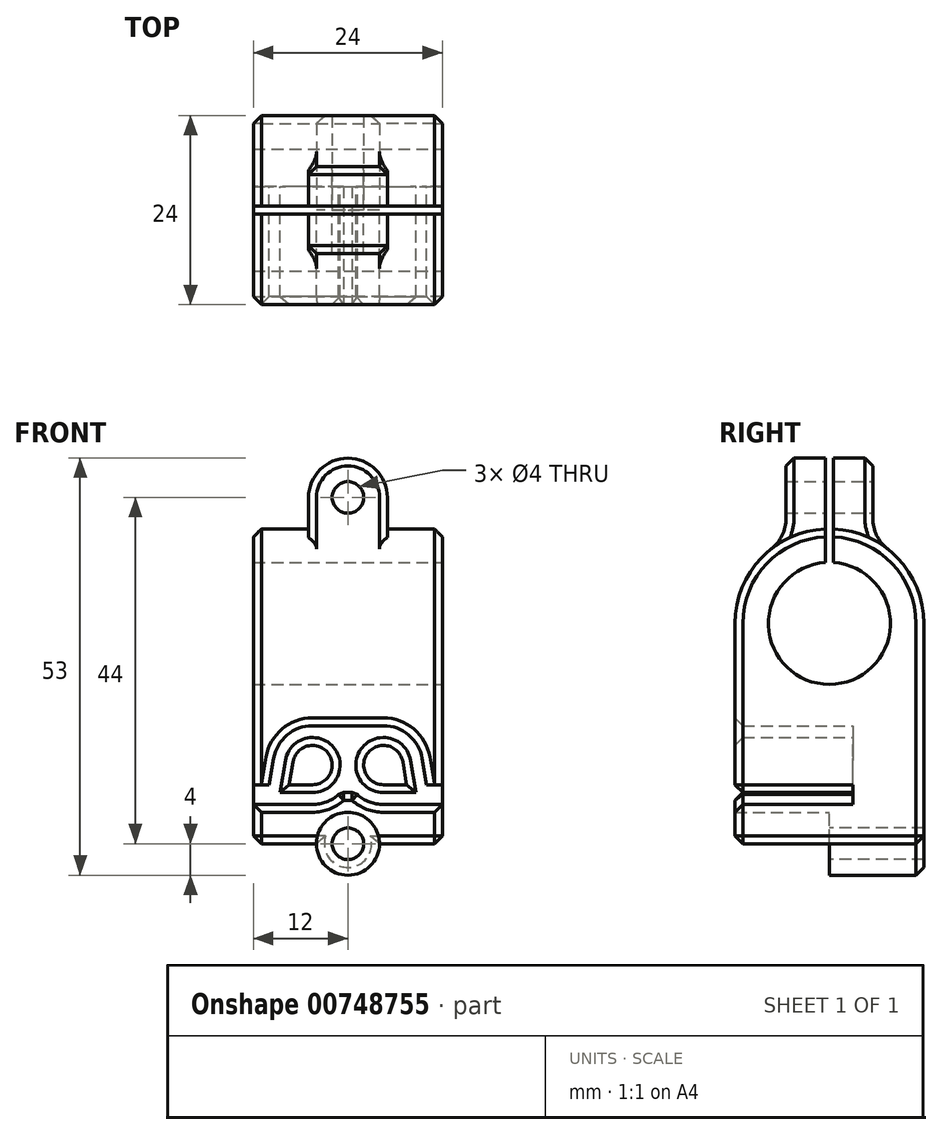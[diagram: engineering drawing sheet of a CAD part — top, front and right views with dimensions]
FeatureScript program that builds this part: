
annotation { "Feature Type Name" : "Feature", "Feature Type Description" : "" }
export const myFeature = defineFeature(function(context is Context, id is Id, definition is map)
    precondition{}
    {
        {
            var Q0;
            Q0=qCreatedBy(makeId("Front.planeOp"),FACE);
            var sketch = newSketch(context, id + "F0", { "sketchPlane" : qUnion([Q0])});
            skCircle(sketch, "E0", {"center": v(0, 0) * mm, "radius": 2 * mm});
            skCircle(sketch, "E1", {"center": v(0, 0) * mm, "radius": 4 * mm});
            skLineSegment(sketch, "E2", {"start": v(0, 0) * mm, "end": v(-12, 0) * mm});
            skLineSegment(sketch, "E3", {"start": v(-12, 0) * mm, "end": v(-12, 40) * mm});
            skLineSegment(sketch, "E4", {"start": v(-12, 40) * mm, "end": v(0, 40) * mm});
            skCircle(sketch, "E5", {"center": v(-4.5, 10) * mm, "radius": 3.5 * mm});
            skLineSegment(sketch, "E6", {"start": v(-12, 7.5) * mm, "end": v(-10, 7.5) * mm});
            skCircle(sketch, "E7", {"center": v(-4.5, 10) * mm, "radius": 5 * mm});
            skLineSegment(sketch, "E8", {"start": v(-4.5, 5) * mm, "end": v(-12, 5) * mm});
            skLineSegment(sketch, "E9", {"start": v(-12, 16) * mm, "end": v(0, 16) * mm});
            skLineSegment(sketch, "E10", {"start": v(0, 49) * mm, "end": v(-5, 49) * mm});
            skLineSegment(sketch, "E11", {"start": v(-5, 49) * mm, "end": v(-5, 40) * mm});
            skCircle(sketch, "E12", {"center": v(0, 44) * mm, "radius": 2 * mm});
            skLineSegment(sketch, "E13", {"start": v(0, 49) * mm, "end": v(0, -4) * mm});
            skLineSegment(sketch, "E14", {"start": v(-12, 28) * mm, "end": v(0, 28) * mm});
            skLineSegment(sketch, "E15", {"start": v(-5, 40) * mm, "end": v(-5, 28) * mm});
            skLineSegment(sketch, "E16", {"start": v(-4.5, 6.5) * mm, "end": v(-8.65, 6.5) * mm});
            skLineSegment(sketch, "E17", {"start": v(-8.65, 6.5) * mm, "end": v(-7.95, 10.59) * mm});
            skLineSegment(sketch, "E18", {"start": v(-10, 7.5) * mm, "end": v(-9.43, 10.84) * mm});
            skLineSegment(sketch, "E19", {"start": v(-4.5, 15) * mm, "end": v(0, 15) * mm});
            skLineSegment(sketch, "E20", {"start": v(-0.93, 6.5) * mm, "end": v(0, 6.5) * mm});
            skSolve(sketch);
        }
        {
            var Q0;
            {var subQ5=sQuery(id+"F0.wireOp",EDGE,"E10");Q0=makeQuery(id+"F0.imprint","IMPRINT",FACE,{"disambiguationData":[TD([[makeQuery(id+"F0.imprint","IMPRINT",EDGE,{"derivedFrom":subQ5}),1.0]])]});}
            var Q1;
            {var subQ3=sQuery(id+"F0.wireOp",EDGE,"E15");Q1=makeQuery(id+"F0.imprint","IMPRINT",FACE,{"disambiguationData":[TD([[makeQuery(id+"F0.imprint","IMPRINT",EDGE,{"derivedFrom":subQ3}),1.0]])]});}
            extrude(context, id + "F1", {"entities" : qUnion([Q0, Q1]), "endBound" : BoundingType.SYMMETRIC, "depth" : 11 * mm, "offsetDistance" : 25 * mm});
        }
        {
            var Q0;
            {var subQ1=sQuery(id+"F0.wireOp",EDGE,"E9");Q0=makeQuery(id+"F0.imprint","IMPRINT",FACE,{"disambiguationData":[TD([[makeQuery(id+"F0.imprint","IMPRINT",EDGE,{"derivedFrom":subQ1}),1.0]])]});}
            var Q1;
            Q1=sQuery(id+"F0.wireOp",EDGE,"E14");
            revolve(context, id + "F2", {"operationType" : NewBodyOperationType.ADD, "surfaceOperationType" : NewSurfaceOperationType.NEW, "entities" : qUnion([Q0]), "axis" : qUnion([Q1]), "revolveType" : RevolveType.FULL});
        }
        {
            var Q0;
            {var subQ1=sQuery(id+"F0.wireOp",EDGE,"E9");Q0=makeQuery(id+"F0.imprint","IMPRINT",FACE,{"disambiguationData":[TD([[makeQuery(id+"F0.imprint","IMPRINT",EDGE,{"derivedFrom":subQ1}),1.0]])]});}
            var Q1;
            {var subQ0=sQuery(id+"F0.wireOp",EDGE,"E6");Q1=makeQuery(id+"F0.imprint","IMPRINT",FACE,{"disambiguationData":[TD([[makeQuery(id+"F0.imprint","IMPRINT",EDGE,{"derivedFrom":subQ0}),1.0]])]});}
            var Q2;
            {var subQ0=sQuery(id+"F0.wireOp",EDGE,"D34r3Q79-cY7r-4sOT-R41t-FvUsecisL4TW");var subQ1=sQuery(id+"F0.wireOp",EDGE,"E5");var subQ2=makeQuery(id+"F0.imprint","INTERSECT",VERTEX,{"derivedFrom":[subQ1,subQ0]});Q2=makeQuery(id+"F0.imprint","IMPRINT",FACE,{"disambiguationData":[TD([[makeQuery(id+"F0.imprint","IMPRINT",EDGE,{"disambiguationData":[TD([[subQ2,1.0]])],"derivedFrom":subQ1}),-1.0]])]});}
            var Q3;
            {var subQ0=sQuery(id+"F0.wireOp",EDGE,"E5");var subQ1=makeQuery(id+"F0.imprint","INTERSECT",VERTEX,{"derivedFrom":[subQ0,sQuery(id+"F0.wireOp",EDGE,"D34r3Q79-cY7r-4sOT-R41t-FvUsecisL4TW")]});Q3=makeQuery(id+"F0.imprint","IMPRINT",FACE,{"disambiguationData":[TD([[makeQuery(id+"F0.imprint","IMPRINT",EDGE,{"disambiguationData":[TD([[subQ1,1.0]])],"derivedFrom":subQ0}),1.0]])]});}
            var Q4;
            {var subQ0=sQuery(id+"F0.wireOp",EDGE,"r9bTKT41-j5EP-3SKQ-5lYN-j0jZzXjLLhCI");var subQ1=sQuery(id+"F0.wireOp",EDGE,"D34r3Q79-cY7r-4sOT-R41t-FvUsecisL4TW");var subQ2=makeQuery(id+"F0.imprint","INTERSECT",VERTEX,{"derivedFrom":[subQ1,subQ0]});Q4=makeQuery(id+"F0.imprint","IMPRINT",FACE,{"disambiguationData":[TD([[makeQuery(id+"F0.imprint","IMPRINT",EDGE,{"disambiguationData":[TD([[subQ2,1.0]])],"derivedFrom":subQ1}),-1.0]])]});}
            var Q5;
            {var subQ3=sQuery(id+"F0.wireOp",EDGE,"E8");Q5=makeQuery(id+"F0.imprint","IMPRINT",FACE,{"disambiguationData":[TD([[makeQuery(id+"F0.imprint","IMPRINT",EDGE,{"derivedFrom":subQ3}),1.0]])]});}
            var Q6;
            {var subQ0=sQuery(id+"F0.wireOp",EDGE,"E17");var subQ1=sQuery(id+"F0.wireOp",EDGE,"E7");var subQ2=makeQuery(id+"F0.imprint","INTERSECT",VERTEX,{"derivedFrom":[subQ1,subQ0]});Q6=makeQuery(id+"F0.imprint","IMPRINT",FACE,{"disambiguationData":[TD([[makeQuery(id+"F0.imprint","IMPRINT",EDGE,{"disambiguationData":[TD([[subQ2,-1.0]])],"derivedFrom":subQ1}),-1.0]])]});}
            extrude(context, id + "F3", {"entities" : qUnion([Q0, Q1, Q2, Q3, Q4, Q5, Q6]), "operationType" : NewBodyOperationType.ADD, "depth" : 12 * mm, "offsetDistance" : 25 * mm});
        }
        {
            var Q0;
            {var subQ0=sQuery(id+"F0.wireOp",EDGE,"E6");Q0=makeQuery(id+"F0.imprint","IMPRINT",FACE,{"disambiguationData":[TD([[makeQuery(id+"F0.imprint","IMPRINT",EDGE,{"derivedFrom":subQ0}),1.0]])]});}
            var Q1;
            {var subQ0=sQuery(id+"F0.wireOp",EDGE,"E5");var subQ1=makeQuery(id+"F0.imprint","INTERSECT",VERTEX,{"derivedFrom":[subQ0,sQuery(id+"F0.wireOp",EDGE,"D34r3Q79-cY7r-4sOT-R41t-FvUsecisL4TW")]});Q1=makeQuery(id+"F0.imprint","IMPRINT",FACE,{"disambiguationData":[TD([[makeQuery(id+"F0.imprint","IMPRINT",EDGE,{"disambiguationData":[TD([[subQ1,1.0]])],"derivedFrom":subQ0}),1.0]])]});}
            var Q2;
            {var subQ1=sQuery(id+"F0.wireOp",EDGE,"E5");var subQ6=sQuery(id+"F0.wireOp",EDGE,"D34r3Q79-cY7r-4sOT-R41t-FvUsecisL4TW");var subQ7=makeQuery(id+"F0.imprint","INTERSECT",VERTEX,{"derivedFrom":[subQ1,subQ6]});Q2=makeQuery(id+"F0.imprint","IMPRINT",FACE,{"disambiguationData":[TD([[makeQuery(id+"F0.imprint","IMPRINT",EDGE,{"disambiguationData":[TD([[subQ7,-1.0]])],"derivedFrom":subQ1}),-1.0]])]});}
            var Q3;
            {var subQ0=sQuery(id+"F0.wireOp",EDGE,"D34r3Q79-cY7r-4sOT-R41t-FvUsecisL4TW");var subQ1=sQuery(id+"F0.wireOp",EDGE,"E5");var subQ2=makeQuery(id+"F0.imprint","INTERSECT",VERTEX,{"derivedFrom":[subQ1,subQ0]});Q3=makeQuery(id+"F0.imprint","IMPRINT",FACE,{"disambiguationData":[TD([[makeQuery(id+"F0.imprint","IMPRINT",EDGE,{"disambiguationData":[TD([[subQ2,1.0]])],"derivedFrom":subQ1}),-1.0]])]});}
            var Q4;
            {var subQ0=sQuery(id+"F0.wireOp",EDGE,"r9bTKT41-j5EP-3SKQ-5lYN-j0jZzXjLLhCI");var subQ1=sQuery(id+"F0.wireOp",EDGE,"D34r3Q79-cY7r-4sOT-R41t-FvUsecisL4TW");var subQ2=makeQuery(id+"F0.imprint","INTERSECT",VERTEX,{"derivedFrom":[subQ1,subQ0]});Q4=makeQuery(id+"F0.imprint","IMPRINT",FACE,{"disambiguationData":[TD([[makeQuery(id+"F0.imprint","IMPRINT",EDGE,{"disambiguationData":[TD([[subQ2,1.0]])],"derivedFrom":subQ1}),-1.0]])]});}
            var Q5;
            {var subQ1=sQuery(id+"F0.wireOp",EDGE,"E9");Q5=makeQuery(id+"F0.imprint","IMPRINT",FACE,{"disambiguationData":[TD([[makeQuery(id+"F0.imprint","IMPRINT",EDGE,{"derivedFrom":subQ1}),1.0]])]});}
            var Q6;
            {var subQ0=sQuery(id+"F0.wireOp",EDGE,"E17");var subQ1=sQuery(id+"F0.wireOp",EDGE,"E7");var subQ2=makeQuery(id+"F0.imprint","INTERSECT",VERTEX,{"derivedFrom":[subQ1,subQ0]});Q6=makeQuery(id+"F0.imprint","IMPRINT",FACE,{"disambiguationData":[TD([[makeQuery(id+"F0.imprint","IMPRINT",EDGE,{"disambiguationData":[TD([[subQ2,-1.0]])],"derivedFrom":subQ1}),-1.0]])]});}
            var Q7;
            {var subQ3=sQuery(id+"F0.wireOp",EDGE,"E8");Q7=makeQuery(id+"F0.imprint","IMPRINT",FACE,{"disambiguationData":[TD([[makeQuery(id+"F0.imprint","IMPRINT",EDGE,{"derivedFrom":subQ3}),1.0]])]});}
            var Q8;
            {var subQ6=sQuery(id+"F0.wireOp",EDGE,"E16");var subQ8=sQuery(id+"F0.wireOp",EDGE,"E5");var subQ9=makeQuery(id+"F0.imprint","INTERSECT",VERTEX,{"derivedFrom":[subQ8,subQ6]});Q8=makeQuery(id+"F0.imprint","IMPRINT",FACE,{"disambiguationData":[TD([[makeQuery(id+"F0.imprint","IMPRINT",EDGE,{"disambiguationData":[TD([[subQ9,-1.0]])],"derivedFrom":subQ8}),-1.0]])]});}
            var Q9;
            {var subQ4=sQuery(id+"F0.wireOp",EDGE,"E6");Q9=makeQuery(id+"F0.imprint","IMPRINT",FACE,{"disambiguationData":[TD([[makeQuery(id+"F0.imprint","IMPRINT",EDGE,{"derivedFrom":subQ4}),-1.0]])]});}
            var Q10;
            {var subQ0=sQuery(id+"F0.wireOp",EDGE,"E2");var subQ1=sQuery(id+"F0.wireOp",EDGE,"E0");var subQ2=makeQuery(id+"F0.imprint","INTERSECT",VERTEX,{"derivedFrom":[subQ1,subQ0]});Q10=makeQuery(id+"F0.imprint","IMPRINT",FACE,{"disambiguationData":[TD([[makeQuery(id+"F0.imprint","IMPRINT",EDGE,{"disambiguationData":[TD([[subQ2,-1.0]])],"derivedFrom":subQ1}),-1.0]])]});}
            var Q11;
            {var subQ0=sQuery(id+"F0.wireOp",EDGE,"E2");var subQ1=sQuery(id+"F0.wireOp",EDGE,"E0");var subQ2=makeQuery(id+"F0.imprint","INTERSECT",VERTEX,{"derivedFrom":[subQ1,subQ0]});Q11=makeQuery(id+"F0.imprint","IMPRINT",FACE,{"disambiguationData":[TD([[makeQuery(id+"F0.imprint","IMPRINT",EDGE,{"disambiguationData":[TD([[subQ2,1.0]])],"derivedFrom":subQ1}),-1.0]])]});}
            var Q12;
            {var subQ0=sQuery(id+"F0.wireOp",EDGE,"E19");Q12=makeQuery(id+"F0.imprint","IMPRINT",FACE,{"disambiguationData":[TD([[makeQuery(id+"F0.imprint","IMPRINT",EDGE,{"derivedFrom":subQ0}),-1.0]])]});}
            var Q13;
            {var subQ0=sQuery(id+"F0.wireOp",EDGE,"E20");Q13=makeQuery(id+"F0.imprint","IMPRINT",FACE,{"disambiguationData":[TD([[makeQuery(id+"F0.imprint","IMPRINT",EDGE,{"derivedFrom":subQ0}),1.0]])]});}
            extrude(context, id + "F4", {"entities" : qUnion([Q0, Q1, Q2, Q3, Q4, Q5, Q6, Q7, Q8, Q9, Q10, Q11, Q12, Q13]), "operationType" : NewBodyOperationType.ADD, "oppositeDirection" : true, "depth" : 12 * mm, "offsetDistance" : 25 * mm});
        }
        {
            var Q0;
            {var subQ4=sQuery(id+"F0.wireOp",EDGE,"E6");Q0=makeQuery(id+"F0.imprint","IMPRINT",FACE,{"disambiguationData":[TD([[makeQuery(id+"F0.imprint","IMPRINT",EDGE,{"derivedFrom":subQ4}),-1.0]])]});}
            var Q1;
            {var subQ6=sQuery(id+"F0.wireOp",EDGE,"E16");var subQ8=sQuery(id+"F0.wireOp",EDGE,"E5");var subQ9=makeQuery(id+"F0.imprint","INTERSECT",VERTEX,{"derivedFrom":[subQ8,subQ6]});Q1=makeQuery(id+"F0.imprint","IMPRINT",FACE,{"disambiguationData":[TD([[makeQuery(id+"F0.imprint","IMPRINT",EDGE,{"disambiguationData":[TD([[subQ9,-1.0]])],"derivedFrom":subQ8}),-1.0]])]});}
            var Q2;
            {var subQ0=sQuery(id+"F0.wireOp",EDGE,"E19");Q2=makeQuery(id+"F0.imprint","IMPRINT",FACE,{"disambiguationData":[TD([[makeQuery(id+"F0.imprint","IMPRINT",EDGE,{"derivedFrom":subQ0}),-1.0]])]});}
            var Q3;
            {var subQ0=sQuery(id+"F0.wireOp",EDGE,"E20");Q3=makeQuery(id+"F0.imprint","IMPRINT",FACE,{"disambiguationData":[TD([[makeQuery(id+"F0.imprint","IMPRINT",EDGE,{"derivedFrom":subQ0}),1.0]])]});}
            extrude(context, id + "F5", {"entities" : qUnion([Q0, Q1, Q2, Q3]), "operationType" : NewBodyOperationType.REMOVE, "oppositeDirection" : true, "depth" : 3 * mm, "offsetDistance" : 25 * mm});
        }
        {
            var Q0;
            {var subQ0=sQuery(id+"F0.wireOp",EDGE,"E13");var subQ1=makeQuery(id+"F0.imprint","INTERSECT",VERTEX,{"disambiguationData":[OD(1.0)],"derivedFrom":[sQuery(id+"F0.wireOp",EDGE,"E1"),subQ0]});var subQ2=makeQuery(id+"F0.imprint","INTERSECT",VERTEX,{"derivedFrom":[sQuery(id+"F0.wireOp",EDGE,"E9"),subQ0]});var subQ4=makeQuery(id+"F0.imprint","INTERSECT",VERTEX,{"derivedFrom":[sQuery(id+"F0.wireOp",EDGE,"E4"),subQ0]});Q0=makeQuery(id+"F4.boolean.opBoolean","MERGE",FACE,{"derivedFrom":[makeQuery(id+"F3.boolean.opBoolean","MERGE",FACE,{"derivedFrom":[makeQuery(id+"F2.boolean.opBoolean","MERGE",FACE,{"derivedFrom":[makeQuery(id+"F1.opExtrude","SWEPT_FACE",FACE,{"disambiguationData":[OSD([subQ0]),TDD([makeQuery(id+"F0.imprint","IMPRINT",EDGE,{"disambiguationData":[TD([[subQ4,1.0]])],"derivedFrom":subQ0}),makeQuery(id+"F0.imprint","IMPRINT",EDGE,{"disambiguationData":[TD([[subQ4,-1.0]])],"derivedFrom":subQ0})])]}),makeQuery(id+"F2.opRevolve","SWEPT_FACE",FACE,{"disambiguationData":[OSD([subQ0])]})]}),makeQuery(id+"F3.opExtrude","SWEPT_FACE",FACE,{"disambiguationData":[OSD([subQ0]),TDD([makeQuery(id+"F0.imprint","IMPRINT",EDGE,{"disambiguationData":[TD([[subQ2,1.0]])],"derivedFrom":subQ0}),makeQuery(id+"F0.imprint","IMPRINT",EDGE,{"disambiguationData":[TD([[subQ2,-1.0]])],"derivedFrom":subQ0}),makeQuery(id+"F0.imprint","IMPRINT",EDGE,{"disambiguationData":[TD([[subQ1,-1.0]])],"derivedFrom":subQ0})])]})]}),makeQuery(id+"F4.opExtrude","SWEPT_FACE",FACE,{"disambiguationData":[OSD([subQ0])]})]});}
            var sketch = newSketch(context, id + "F6", { "sketchPlane" : qUnion([Q0])});
            skCircle(sketch, "E21", {"center": v(0, 28) * mm, "radius": 7.75 * mm});
            skLineSegment(sketch, "E22", {"start": v(0, 28) * mm, "end": v(0, 58) * mm});
            skLineSegment(sketch, "E23", {"start": v(0, 58) * mm, "end": v(-0.5, 58) * mm});
            skLineSegment(sketch, "E24", {"start": v(-0.5, 58) * mm, "end": v(-0.5, 28) * mm});
            skLineSegment(sketch, "E25", {"start": v(-0.5, 28) * mm, "end": v(0, 28) * mm});
            skLineSegment(sketch, "E26", {"start": v(0.5, 28) * mm, "end": v(0.5, 58) * mm});
            skLineSegment(sketch, "E27", {"start": v(0.5, 58) * mm, "end": v(0, 58) * mm});
            skLineSegment(sketch, "E28", {"start": v(0, 28) * mm, "end": v(0.5, 28) * mm});
            skSolve(sketch);
        }
        {
            var Q0;
            Q0 = qSketchRegion(id + "F6", true);
            extrude(context, id + "F7", {"entities" : qUnion([Q0]), "operationType" : NewBodyOperationType.REMOVE, "oppositeDirection" : true, "depth" : 12 * mm, "offsetDistance" : 25 * mm});
        }
        {
            var Q0;
            {var subQ0=sQuery(id+"F0.wireOp",EDGE,"E10");var subQ2=sQuery(id+"F0.wireOp",EDGE,"E11");Q0=makeQuery(id+"F7.boolean.opBoolean","SPLIT",EDGE,{"disambiguationData":[TD([makeQuery(id+"F7.opExtrude","SWEPT_FACE",FACE,{"disambiguationData":[OSD([sQuery(id+"F6.wireOp",EDGE,"E24")])]})])],"derivedFrom":makeQuery(id+"F1.opExtrude","SWEPT_EDGE",EDGE,{"disambiguationData":[OSD([subQ0,subQ2])]})});}
            var Q1;
            {var subQ0=sQuery(id+"F0.wireOp",EDGE,"E10");var subQ2=sQuery(id+"F0.wireOp",EDGE,"E11");Q1=makeQuery(id+"F7.boolean.opBoolean","SPLIT",EDGE,{"disambiguationData":[TD([makeQuery(id+"F7.opExtrude","SWEPT_FACE",FACE,{"disambiguationData":[OSD([sQuery(id+"F6.wireOp",EDGE,"E26")])]})])],"derivedFrom":makeQuery(id+"F1.opExtrude","SWEPT_EDGE",EDGE,{"disambiguationData":[OSD([subQ0,subQ2])]})});}
            fillet(context, id + "F8", {"entities" : qUnion([Q0, Q1]), "radius" : 5 * mm, "tangentPropagation" : true, "allowEdgeOverflow" : false});
        }
        {
            var Q0;
            Q0=makeQuery(id+"F2.boolean.opBoolean","INTERSECT",EDGE,{"derivedFrom":[makeQuery(id+"F1.opExtrude","CAP_FACE",FACE,{"disambiguationData":[OSD([sQuery(id+"F0.wireOp",EDGE,"E10"),sQuery(id+"F0.wireOp",EDGE,"E11"),sQuery(id+"F0.wireOp",EDGE,"E12"),sQuery(id+"F0.wireOp",EDGE,"E13"),sQuery(id+"F0.wireOp",EDGE,"E14"),sQuery(id+"F0.wireOp",EDGE,"E15")])],"isStart":false}),makeQuery(id+"F2.opRevolve","SWEPT_FACE",FACE,{"disambiguationData":[OSD([sQuery(id+"F0.wireOp",EDGE,"E9")])]})]});
            var Q1;
            Q1=makeQuery(id+"F2.boolean.opBoolean","INTERSECT",EDGE,{"derivedFrom":[makeQuery(id+"F1.opExtrude","CAP_FACE",FACE,{"disambiguationData":[OSD([sQuery(id+"F0.wireOp",EDGE,"E10"),sQuery(id+"F0.wireOp",EDGE,"E11"),sQuery(id+"F0.wireOp",EDGE,"E12"),sQuery(id+"F0.wireOp",EDGE,"E13"),sQuery(id+"F0.wireOp",EDGE,"E14"),sQuery(id+"F0.wireOp",EDGE,"E15")])],"isStart":true}),makeQuery(id+"F2.opRevolve","SWEPT_FACE",FACE,{"disambiguationData":[OSD([sQuery(id+"F0.wireOp",EDGE,"E9")])]})]});
            fillet(context, id + "F9", {"entities" : qUnion([Q0, Q1]), "radius" : 5 * mm, "tangentPropagation" : true, "allowEdgeOverflow" : false});
        }
        {
            var Q0;
            Q0=makeQuery(id+"F1.opExtrude","CAP_EDGE",EDGE,{"disambiguationData":[OSD([sQuery(id+"F0.wireOp",EDGE,"E11"),sQuery(id+"F0.wireOp",EDGE,"E15")])],"isStart":true});
            var Q1;
            {var subQ0=sQuery(id+"F0.wireOp",EDGE,"E15");var subQ1=sQuery(id+"F0.wireOp",EDGE,"E11");var subQ2=sQuery(id+"F0.wireOp",EDGE,"E10");var subQ3=makeQuery(id+"F1.opExtrude","CAP_FACE",FACE,{"disambiguationData":[OSD([subQ2,subQ1,sQuery(id+"F0.wireOp",EDGE,"E12"),sQuery(id+"F0.wireOp",EDGE,"E13"),sQuery(id+"F0.wireOp",EDGE,"E14"),subQ0])],"isStart":true});Q1=makeQuery(id+"F8.opFillet","BLEND_EDGE",EDGE,{"blendedFrom":[makeQuery(id+"F7.boolean.opBoolean","SPLIT",EDGE,{"disambiguationData":[TD([makeQuery(id+"F7.opExtrude","SWEPT_FACE",FACE,{"disambiguationData":[OSD([sQuery(id+"F6.wireOp",EDGE,"E26")])]})])],"derivedFrom":makeQuery(id+"F1.opExtrude","SWEPT_EDGE",EDGE,{"disambiguationData":[OSD([subQ2,subQ1])]})}),subQ3],"blendedInto":[subQ3]});}
            var Q2;
            {var subQ0=sQuery(id+"F0.wireOp",EDGE,"E15");var subQ1=sQuery(id+"F0.wireOp",EDGE,"E11");var subQ2=sQuery(id+"F0.wireOp",EDGE,"E10");var subQ3=makeQuery(id+"F1.opExtrude","CAP_FACE",FACE,{"disambiguationData":[OSD([subQ2,subQ1,sQuery(id+"F0.wireOp",EDGE,"E12"),sQuery(id+"F0.wireOp",EDGE,"E13"),sQuery(id+"F0.wireOp",EDGE,"E14"),subQ0])],"isStart":false});Q2=makeQuery(id+"F8.opFillet","BLEND_EDGE",EDGE,{"blendedFrom":[makeQuery(id+"F7.boolean.opBoolean","SPLIT",EDGE,{"disambiguationData":[TD([makeQuery(id+"F7.opExtrude","SWEPT_FACE",FACE,{"disambiguationData":[OSD([sQuery(id+"F6.wireOp",EDGE,"E24")])]})])],"derivedFrom":makeQuery(id+"F1.opExtrude","SWEPT_EDGE",EDGE,{"disambiguationData":[OSD([subQ2,subQ1])]})}),subQ3],"blendedInto":[subQ3]});}
            var Q3;
            Q3=makeQuery(id+"F1.opExtrude","CAP_EDGE",EDGE,{"disambiguationData":[OSD([sQuery(id+"F0.wireOp",EDGE,"E11"),sQuery(id+"F0.wireOp",EDGE,"E15")])],"isStart":false});
            var Q4;
            {var subQ0=sQuery(id+"F0.wireOp",EDGE,"E9");var subQ1=sQuery(id+"F0.wireOp",EDGE,"E3");Q4=makeQuery(id+"F7.boolean.opBoolean","SPLIT",EDGE,{"disambiguationData":[TD([makeQuery(id+"F7.opExtrude","SWEPT_FACE",FACE,{"disambiguationData":[OSD([sQuery(id+"F6.wireOp",EDGE,"E24")])]})])],"derivedFrom":makeQuery(id+"F2.opRevolve","SWEPT_EDGE",EDGE,{"disambiguationData":[OSD([subQ1,subQ0])]})});}
            var Q5;
            {var subQ0=sQuery(id+"F0.wireOp",EDGE,"E3");var subQ1=makeQuery(id+"F0.imprint","INTERSECT",VERTEX,{"derivedFrom":[subQ0,sQuery(id+"F0.wireOp",EDGE,"E9")]});Q5=makeQuery(id+"F3.opExtrude","CAP_EDGE",EDGE,{"disambiguationData":[OSD([subQ0]),TDD([makeQuery(id+"F0.imprint","IMPRINT",EDGE,{"disambiguationData":[TD([[makeQuery(id+"F0.imprint","INTERSECT",VERTEX,{"derivedFrom":[subQ0,sQuery(id+"F0.wireOp",EDGE,"E6")]}),-1.0]])],"derivedFrom":subQ0}),makeQuery(id+"F0.imprint","IMPRINT",EDGE,{"disambiguationData":[TD([[subQ1,-1.0]])],"derivedFrom":subQ0})])],"isStart":false});}
            var Q6;
            {var subQ0=sQuery(id+"F0.wireOp",EDGE,"E9");var subQ1=sQuery(id+"F0.wireOp",EDGE,"E3");Q6=makeQuery(id+"F7.boolean.opBoolean","SPLIT",EDGE,{"disambiguationData":[TD([makeQuery(id+"F7.opExtrude","SWEPT_FACE",FACE,{"disambiguationData":[OSD([sQuery(id+"F6.wireOp",EDGE,"E26")])]})])],"derivedFrom":makeQuery(id+"F2.opRevolve","SWEPT_EDGE",EDGE,{"disambiguationData":[OSD([subQ1,subQ0])]})});}
            var Q7;
            Q7=makeQuery(id+"F4.opExtrude","CAP_EDGE",EDGE,{"disambiguationData":[OSD([sQuery(id+"F0.wireOp",EDGE,"E3")])],"isStart":false});
            var Q8;
            {var subQ0=sQuery(id+"F0.wireOp",EDGE,"E3");Q8=makeQuery(id+"F3.opExtrude","CAP_EDGE",EDGE,{"disambiguationData":[OSD([subQ0]),TDD([makeQuery(id+"F0.imprint","IMPRINT",EDGE,{"disambiguationData":[TD([[makeQuery(id+"F0.imprint","INTERSECT",VERTEX,{"derivedFrom":[sQuery(id+"F0.wireOp",EDGE,"E2"),subQ0]}),-1.0]])],"derivedFrom":subQ0})])],"isStart":false});}
            var Q9;
            {var subQ0=sQuery(id+"F0.wireOp",EDGE,"E3");var subQ1=sQuery(id+"F0.wireOp",EDGE,"E2");Q9=makeQuery(id+"F4.boolean.opBoolean","MERGE",EDGE,{"derivedFrom":[makeQuery(id+"F3.opExtrude","SWEPT_EDGE",EDGE,{"disambiguationData":[OSD([subQ1,subQ0])]}),makeQuery(id+"F4.opExtrude","SWEPT_EDGE",EDGE,{"disambiguationData":[OSD([subQ1,subQ0])]})]});}
            var Q10;
            Q10=makeQuery(id+"F3.opExtrude","CAP_EDGE",EDGE,{"disambiguationData":[OSD([sQuery(id+"F0.wireOp",EDGE,"E17")])],"isStart":false});
            var Q11;
            Q11=makeQuery(id+"F3.opExtrude","CAP_EDGE",EDGE,{"disambiguationData":[OSD([sQuery(id+"F0.wireOp",EDGE,"E16")])],"isStart":false});
            var Q12;
            Q12=makeQuery(id+"F3.opExtrude","CAP_EDGE",EDGE,{"disambiguationData":[OSD([sQuery(id+"F0.wireOp",EDGE,"E5")])],"isStart":false});
            var Q13;
            {var subQ0=sQuery(id+"F0.wireOp",EDGE,"E7");Q13=makeQuery(id+"F3.opExtrude","CAP_EDGE",EDGE,{"disambiguationData":[OSD([subQ0]),TDD([makeQuery(id+"F0.imprint","IMPRINT",EDGE,{"disambiguationData":[TD([[makeQuery(id+"F0.imprint","INTERSECT",VERTEX,{"derivedFrom":[subQ0,sQuery(id+"F0.wireOp",EDGE,"E18")]}),1.0]])],"derivedFrom":subQ0})])],"isStart":false});}
            var Q14;
            {var subQ0=sQuery(id+"F0.wireOp",EDGE,"E7");Q14=makeQuery(id+"F3.opExtrude","CAP_EDGE",EDGE,{"disambiguationData":[OSD([subQ0]),TDD([makeQuery(id+"F0.imprint","IMPRINT",EDGE,{"disambiguationData":[TD([[makeQuery(id+"F0.imprint","INTERSECT",VERTEX,{"derivedFrom":[subQ0,sQuery(id+"F0.wireOp",EDGE,"E8")]}),-1.0]])],"derivedFrom":subQ0})])],"isStart":false});}
            var Q15;
            Q15=makeQuery(id+"F3.opExtrude","CAP_EDGE",EDGE,{"disambiguationData":[OSD([sQuery(id+"F0.wireOp",EDGE,"E8")])],"isStart":false});
            var Q16;
            Q16=makeQuery(id+"F3.opExtrude","CAP_EDGE",EDGE,{"disambiguationData":[OSD([sQuery(id+"F0.wireOp",EDGE,"E2")])],"isStart":false});
            var Q17;
            Q17=makeQuery(id+"F4.opExtrude","CAP_EDGE",EDGE,{"disambiguationData":[OSD([sQuery(id+"F0.wireOp",EDGE,"E2")])],"isStart":false});
            var Q18;
            Q18=makeQuery(id+"F4.opExtrude","CAP_EDGE",EDGE,{"disambiguationData":[OSD([sQuery(id+"F0.wireOp",EDGE,"E1")])],"isStart":false});
            var Q19;
            Q19=makeQuery(id+"F3.opExtrude","CAP_EDGE",EDGE,{"disambiguationData":[OSD([sQuery(id+"F0.wireOp",EDGE,"E19")])],"isStart":false});
            var Q20;
            Q20=makeQuery(id+"F3.opExtrude","CAP_EDGE",EDGE,{"disambiguationData":[OSD([sQuery(id+"F0.wireOp",EDGE,"E18")])],"isStart":false});
            var Q21;
            Q21=makeQuery(id+"F3.opExtrude","CAP_EDGE",EDGE,{"disambiguationData":[OSD([sQuery(id+"F0.wireOp",EDGE,"E20")])],"isStart":false});
            var Q22;
            {var subQ0=sQuery(id+"F0.wireOp",EDGE,"E20");var subQ1=sQuery(id+"F0.wireOp",EDGE,"E7");Q22=makeQuery(id+"F5.boolean.opBoolean","MERGE",EDGE,{"derivedFrom":[makeQuery(id+"F3.opExtrude","SWEPT_EDGE",EDGE,{"disambiguationData":[OSD([subQ1,subQ0])]}),makeQuery(id+"F5.opExtrude","SWEPT_EDGE",EDGE,{"disambiguationData":[OSD([subQ1,subQ0])]})]});}
            var Q23;
            {var subQ0=sQuery(id+"F0.wireOp",EDGE,"E10");var subQ1=sQuery(id+"F0.wireOp",EDGE,"E15");var subQ2=sQuery(id+"F0.wireOp",EDGE,"E11");var subQ3=makeQuery(id+"F1.opExtrude","CAP_FACE",FACE,{"disambiguationData":[OSD([subQ0,subQ2,sQuery(id+"F0.wireOp",EDGE,"E12"),sQuery(id+"F0.wireOp",EDGE,"E13"),sQuery(id+"F0.wireOp",EDGE,"E14"),subQ1])],"isStart":false});var subQ4=makeQuery(id+"F2.opRevolve","SWEPT_FACE",FACE,{"disambiguationData":[OSD([sQuery(id+"F0.wireOp",EDGE,"E9")])]});Q23=makeQuery(id+"F9.opFillet","BLEND_EDGE",EDGE,{"blendedFrom":[makeQuery(id+"F2.boolean.opBoolean","INTERSECT",EDGE,{"derivedFrom":[subQ3,subQ4]}),makeQuery(id+"F7.boolean.opBoolean","SPLIT",FACE,{"disambiguationData":[TD([makeQuery(id+"F7.opExtrude","SWEPT_FACE",FACE,{"disambiguationData":[OSD([sQuery(id+"F6.wireOp",EDGE,"E24")])]})])],"derivedFrom":makeQuery(id+"F1.opExtrude","SWEPT_FACE",FACE,{"disambiguationData":[OSD([subQ2,subQ1])]})})],"blendedInto":[makeQuery(id+"F7.boolean.opBoolean","SPLIT",FACE,{"disambiguationData":[TD([makeQuery(id+"F7.opExtrude","SWEPT_FACE",FACE,{"disambiguationData":[OSD([sQuery(id+"F6.wireOp",EDGE,"E24")])]})])],"derivedFrom":makeQuery(id+"F1.opExtrude","SWEPT_FACE",FACE,{"disambiguationData":[OSD([subQ2,subQ1])]})})]});}
            var Q24;
            {var subQ0=sQuery(id+"F0.wireOp",EDGE,"E10");var subQ1=sQuery(id+"F0.wireOp",EDGE,"E15");var subQ2=sQuery(id+"F0.wireOp",EDGE,"E11");var subQ3=makeQuery(id+"F1.opExtrude","CAP_FACE",FACE,{"disambiguationData":[OSD([subQ0,subQ2,sQuery(id+"F0.wireOp",EDGE,"E12"),sQuery(id+"F0.wireOp",EDGE,"E13"),sQuery(id+"F0.wireOp",EDGE,"E14"),subQ1])],"isStart":true});var subQ4=makeQuery(id+"F2.opRevolve","SWEPT_FACE",FACE,{"disambiguationData":[OSD([sQuery(id+"F0.wireOp",EDGE,"E9")])]});Q24=makeQuery(id+"F9.opFillet","BLEND_EDGE",EDGE,{"blendedFrom":[makeQuery(id+"F2.boolean.opBoolean","INTERSECT",EDGE,{"derivedFrom":[subQ3,subQ4]}),makeQuery(id+"F7.boolean.opBoolean","SPLIT",FACE,{"disambiguationData":[TD([makeQuery(id+"F7.opExtrude","SWEPT_FACE",FACE,{"disambiguationData":[OSD([sQuery(id+"F6.wireOp",EDGE,"E26")])]})])],"derivedFrom":makeQuery(id+"F1.opExtrude","SWEPT_FACE",FACE,{"disambiguationData":[OSD([subQ2,subQ1])]})})],"blendedInto":[makeQuery(id+"F7.boolean.opBoolean","SPLIT",FACE,{"disambiguationData":[TD([makeQuery(id+"F7.opExtrude","SWEPT_FACE",FACE,{"disambiguationData":[OSD([sQuery(id+"F6.wireOp",EDGE,"E26")])]})])],"derivedFrom":makeQuery(id+"F1.opExtrude","SWEPT_FACE",FACE,{"disambiguationData":[OSD([subQ2,subQ1])]})})]});}
            chamfer(context, id + "F10", {"entities" : qUnion([Q0, Q1, Q2, Q3, Q4, Q5, Q6, Q7, Q8, Q9, Q10, Q11, Q12, Q13, Q14, Q15, Q16, Q17, Q18, Q19, Q20, Q21, Q22, Q23, Q24]), "width" : 1 * mm});
        }
        {
            var Q0;
            Q0=makeQuery(id+"F1.opExtrude","SWEPT_BODY",BODY,{"disambiguationData":[OSD([sQuery(id+"F0.wireOp",EDGE,"E10"),sQuery(id+"F0.wireOp",EDGE,"E11"),sQuery(id+"F0.wireOp",EDGE,"E12"),sQuery(id+"F0.wireOp",EDGE,"E13"),sQuery(id+"F0.wireOp",EDGE,"E14"),sQuery(id+"F0.wireOp",EDGE,"E15")])]});
            var Q1;
            {var subQ0=sQuery(id+"F0.wireOp",EDGE,"E13");Q1=makeQuery(id+"F6.imprint","IMPRINT",FACE,{"disambiguationData":[TD([[makeQuery(id+"F6.imprint","IMPRINT",EDGE,{"derivedFrom":makeQuery(id+"F4.opExtrude","CAP_EDGE",EDGE,{"disambiguationData":[OSD([subQ0])],"isStart":false})}),-1.0]])]});}
            mirror(context, id + "F11", {"operationType" : NewBodyOperationType.ADD, "entities" : qUnion([Q0]), "mirrorPlane" : qUnion([Q1])});
        }
    });
